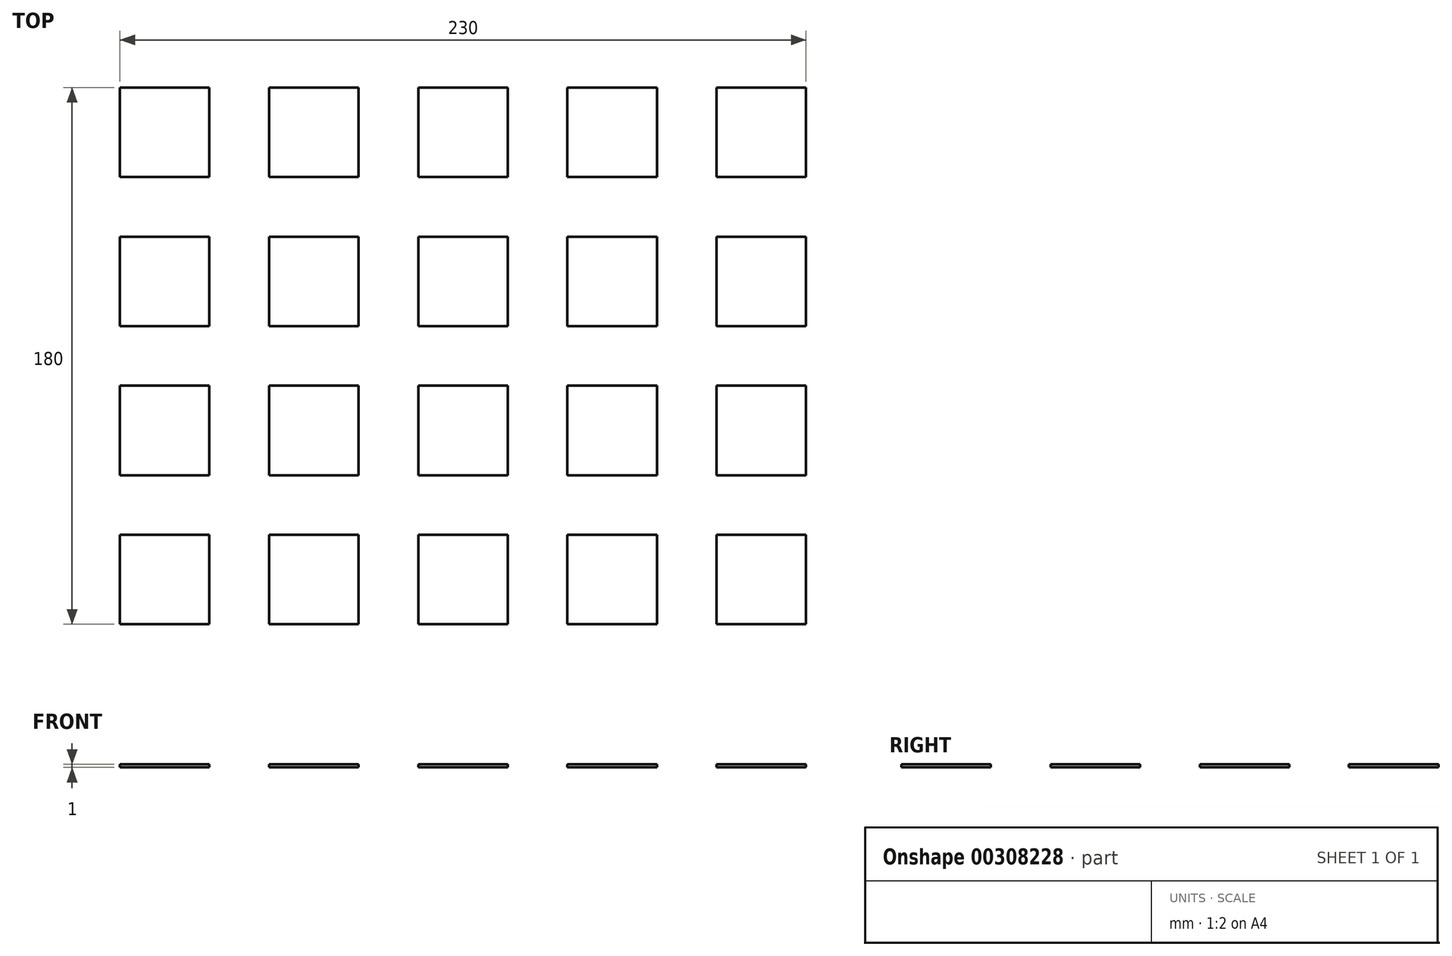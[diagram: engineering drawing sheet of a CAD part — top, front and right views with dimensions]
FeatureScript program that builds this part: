
annotation { "Feature Type Name" : "Feature", "Feature Type Description" : "" }
export const myFeature = defineFeature(function(context is Context, id is Id, definition is map)
    precondition{}
    {
        {
            var Q0;
            Q0=qCreatedBy(makeId("Top.planeOp"),FACE);
            var sketch = newSketch(context, id + "F0", { "sketchPlane" : qUnion([Q0])});
            skLineSegment(sketch, "E0.bottom", {"start": v(10, 10) * mm, "end": v(40, 10) * mm});
            skLineSegment(sketch, "E0.top", {"start": v(10, 40) * mm, "end": v(40, 40) * mm});
            skLineSegment(sketch, "E0.left", {"start": v(10, 40) * mm, "end": v(10, 10) * mm});
            skLineSegment(sketch, "E0.right", {"start": v(40, 40) * mm, "end": v(40, 10) * mm});
            skLineSegment(sketch, "E1.0.1.0", {"start": v(40, 90) * mm, "end": v(40, 60) * mm});
            skLineSegment(sketch, "E1.0.1.1", {"start": v(10, 90) * mm, "end": v(10, 60) * mm});
            skLineSegment(sketch, "E1.0.1.2", {"start": v(10, 60) * mm, "end": v(40, 60) * mm});
            skLineSegment(sketch, "E1.0.1.3", {"start": v(10, 90) * mm, "end": v(40, 90) * mm});
            skLineSegment(sketch, "E1.0.2.0", {"start": v(40, 140) * mm, "end": v(40, 110) * mm});
            skLineSegment(sketch, "E1.0.2.1", {"start": v(10, 140) * mm, "end": v(10, 110) * mm});
            skLineSegment(sketch, "E1.0.2.2", {"start": v(10, 110) * mm, "end": v(40, 110) * mm});
            skLineSegment(sketch, "E1.0.2.3", {"start": v(10, 140) * mm, "end": v(40, 140) * mm});
            skLineSegment(sketch, "E1.0.3.0", {"start": v(40, 190) * mm, "end": v(40, 160) * mm});
            skLineSegment(sketch, "E1.0.3.1", {"start": v(10, 190) * mm, "end": v(10, 160) * mm});
            skLineSegment(sketch, "E1.0.3.2", {"start": v(10, 160) * mm, "end": v(40, 160) * mm});
            skLineSegment(sketch, "E1.0.3.3", {"start": v(10, 190) * mm, "end": v(40, 190) * mm});
            skLineSegment(sketch, "E1.1.0.0", {"start": v(90, 40) * mm, "end": v(90, 10) * mm});
            skLineSegment(sketch, "E1.1.0.1", {"start": v(60, 40) * mm, "end": v(60, 10) * mm});
            skLineSegment(sketch, "E1.1.0.2", {"start": v(60, 10) * mm, "end": v(90, 10) * mm});
            skLineSegment(sketch, "E1.1.0.3", {"start": v(60, 40) * mm, "end": v(90, 40) * mm});
            skLineSegment(sketch, "E1.1.1.0", {"start": v(90, 90) * mm, "end": v(90, 60) * mm});
            skLineSegment(sketch, "E1.1.1.1", {"start": v(60, 90) * mm, "end": v(60, 60) * mm});
            skLineSegment(sketch, "E1.1.1.2", {"start": v(60, 60) * mm, "end": v(90, 60) * mm});
            skLineSegment(sketch, "E1.1.1.3", {"start": v(60, 90) * mm, "end": v(90, 90) * mm});
            skLineSegment(sketch, "E1.1.2.0", {"start": v(90, 140) * mm, "end": v(90, 110) * mm});
            skLineSegment(sketch, "E1.1.2.1", {"start": v(60, 140) * mm, "end": v(60, 110) * mm});
            skLineSegment(sketch, "E1.1.2.2", {"start": v(60, 110) * mm, "end": v(90, 110) * mm});
            skLineSegment(sketch, "E1.1.2.3", {"start": v(60, 140) * mm, "end": v(90, 140) * mm});
            skLineSegment(sketch, "E1.1.3.0", {"start": v(90, 190) * mm, "end": v(90, 160) * mm});
            skLineSegment(sketch, "E1.1.3.1", {"start": v(60, 190) * mm, "end": v(60, 160) * mm});
            skLineSegment(sketch, "E1.1.3.2", {"start": v(60, 160) * mm, "end": v(90, 160) * mm});
            skLineSegment(sketch, "E1.1.3.3", {"start": v(60, 190) * mm, "end": v(90, 190) * mm});
            skLineSegment(sketch, "E1.2.0.0", {"start": v(140, 40) * mm, "end": v(140, 10) * mm});
            skLineSegment(sketch, "E1.2.0.1", {"start": v(110, 40) * mm, "end": v(110, 10) * mm});
            skLineSegment(sketch, "E1.2.0.2", {"start": v(110, 10) * mm, "end": v(140, 10) * mm});
            skLineSegment(sketch, "E1.2.0.3", {"start": v(110, 40) * mm, "end": v(140, 40) * mm});
            skLineSegment(sketch, "E1.2.1.0", {"start": v(140, 90) * mm, "end": v(140, 60) * mm});
            skLineSegment(sketch, "E1.2.1.1", {"start": v(110, 90) * mm, "end": v(110, 60) * mm});
            skLineSegment(sketch, "E1.2.1.2", {"start": v(110, 60) * mm, "end": v(140, 60) * mm});
            skLineSegment(sketch, "E1.2.1.3", {"start": v(110, 90) * mm, "end": v(140, 90) * mm});
            skLineSegment(sketch, "E1.2.2.0", {"start": v(140, 140) * mm, "end": v(140, 110) * mm});
            skLineSegment(sketch, "E1.2.2.1", {"start": v(110, 140) * mm, "end": v(110, 110) * mm});
            skLineSegment(sketch, "E1.2.2.2", {"start": v(110, 110) * mm, "end": v(140, 110) * mm});
            skLineSegment(sketch, "E1.2.2.3", {"start": v(110, 140) * mm, "end": v(140, 140) * mm});
            skLineSegment(sketch, "E1.2.3.0", {"start": v(140, 190) * mm, "end": v(140, 160) * mm});
            skLineSegment(sketch, "E1.2.3.1", {"start": v(110, 190) * mm, "end": v(110, 160) * mm});
            skLineSegment(sketch, "E1.2.3.2", {"start": v(110, 160) * mm, "end": v(140, 160) * mm});
            skLineSegment(sketch, "E1.2.3.3", {"start": v(110, 190) * mm, "end": v(140, 190) * mm});
            skLineSegment(sketch, "E1.3.0.0", {"start": v(190, 40) * mm, "end": v(190, 10) * mm});
            skLineSegment(sketch, "E1.3.0.1", {"start": v(160, 40) * mm, "end": v(160, 10) * mm});
            skLineSegment(sketch, "E1.3.0.2", {"start": v(160, 10) * mm, "end": v(190, 10) * mm});
            skLineSegment(sketch, "E1.3.0.3", {"start": v(160, 40) * mm, "end": v(190, 40) * mm});
            skLineSegment(sketch, "E1.3.1.0", {"start": v(190, 90) * mm, "end": v(190, 60) * mm});
            skLineSegment(sketch, "E1.3.1.1", {"start": v(160, 90) * mm, "end": v(160, 60) * mm});
            skLineSegment(sketch, "E1.3.1.2", {"start": v(160, 60) * mm, "end": v(190, 60) * mm});
            skLineSegment(sketch, "E1.3.1.3", {"start": v(160, 90) * mm, "end": v(190, 90) * mm});
            skLineSegment(sketch, "E1.3.2.0", {"start": v(190, 140) * mm, "end": v(190, 110) * mm});
            skLineSegment(sketch, "E1.3.2.1", {"start": v(160, 140) * mm, "end": v(160, 110) * mm});
            skLineSegment(sketch, "E1.3.2.2", {"start": v(160, 110) * mm, "end": v(190, 110) * mm});
            skLineSegment(sketch, "E1.3.2.3", {"start": v(160, 140) * mm, "end": v(190, 140) * mm});
            skLineSegment(sketch, "E1.3.3.0", {"start": v(190, 190) * mm, "end": v(190, 160) * mm});
            skLineSegment(sketch, "E1.3.3.1", {"start": v(160, 190) * mm, "end": v(160, 160) * mm});
            skLineSegment(sketch, "E1.3.3.2", {"start": v(160, 160) * mm, "end": v(190, 160) * mm});
            skLineSegment(sketch, "E1.3.3.3", {"start": v(160, 190) * mm, "end": v(190, 190) * mm});
            skLineSegment(sketch, "E1.4.0.0", {"start": v(240, 40) * mm, "end": v(240, 10) * mm});
            skLineSegment(sketch, "E1.4.0.1", {"start": v(210, 40) * mm, "end": v(210, 10) * mm});
            skLineSegment(sketch, "E1.4.0.2", {"start": v(210, 10) * mm, "end": v(240, 10) * mm});
            skLineSegment(sketch, "E1.4.0.3", {"start": v(210, 40) * mm, "end": v(240, 40) * mm});
            skLineSegment(sketch, "E1.4.1.0", {"start": v(240, 90) * mm, "end": v(240, 60) * mm});
            skLineSegment(sketch, "E1.4.1.1", {"start": v(210, 90) * mm, "end": v(210, 60) * mm});
            skLineSegment(sketch, "E1.4.1.2", {"start": v(210, 60) * mm, "end": v(240, 60) * mm});
            skLineSegment(sketch, "E1.4.1.3", {"start": v(210, 90) * mm, "end": v(240, 90) * mm});
            skLineSegment(sketch, "E1.4.2.0", {"start": v(240, 140) * mm, "end": v(240, 110) * mm});
            skLineSegment(sketch, "E1.4.2.1", {"start": v(210, 140) * mm, "end": v(210, 110) * mm});
            skLineSegment(sketch, "E1.4.2.2", {"start": v(210, 110) * mm, "end": v(240, 110) * mm});
            skLineSegment(sketch, "E1.4.2.3", {"start": v(210, 140) * mm, "end": v(240, 140) * mm});
            skLineSegment(sketch, "E1.4.3.0", {"start": v(240, 190) * mm, "end": v(240, 160) * mm});
            skLineSegment(sketch, "E1.4.3.1", {"start": v(210, 190) * mm, "end": v(210, 160) * mm});
            skLineSegment(sketch, "E1.4.3.2", {"start": v(210, 160) * mm, "end": v(240, 160) * mm});
            skLineSegment(sketch, "E1.4.3.3", {"start": v(210, 190) * mm, "end": v(240, 190) * mm});
            skLineSegment(sketch, "E1.direction1", {"start": v(10, 40) * mm, "end": v(60, 40) * mm, "construction": true});
            skLineSegment(sketch, "E1.direction2", {"start": v(10, 40) * mm, "end": v(10, 90) * mm, "construction": true});
            skSolve(sketch);
        }
        {
            var Q0;
            Q0=qSketchRegion(id+"F0",true);
            extrude(context, id + "F1", {"entities" : qUnion([Q0]), "depth" : 1 * mm});
        }
    });
